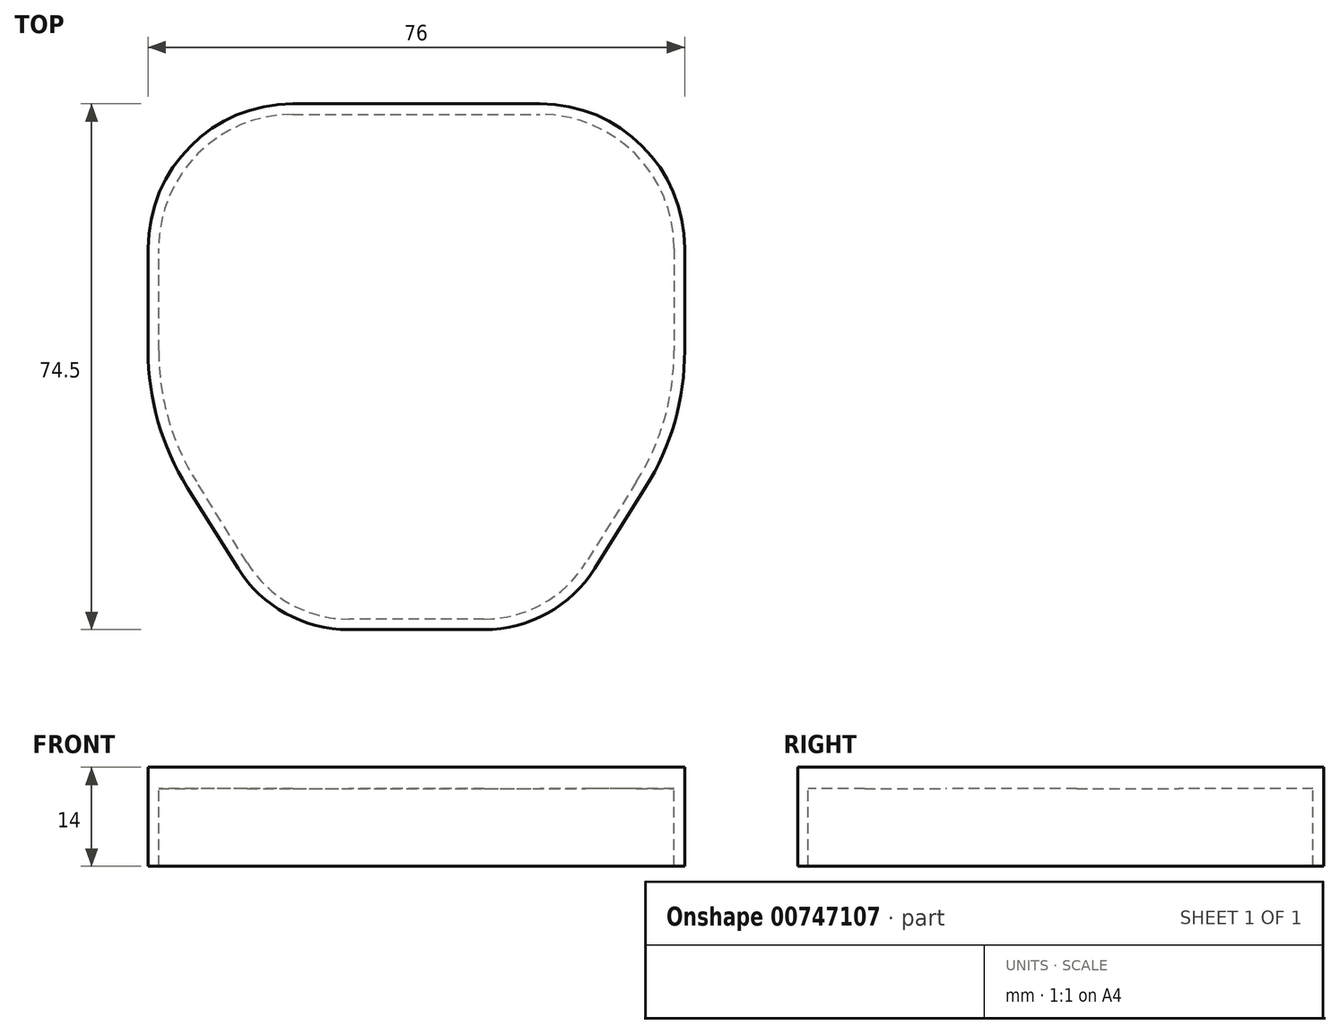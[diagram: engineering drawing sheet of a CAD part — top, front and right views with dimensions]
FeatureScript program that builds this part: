
annotation { "Feature Type Name" : "Feature", "Feature Type Description" : "" }
export const myFeature = defineFeature(function(context is Context, id is Id, definition is map)
    precondition{}
    {
        {
            var Q0;
            Q0=qCreatedBy(makeId("Top.planeOp"),FACE);
            var sketch = newSketch(context, id + "F0", { "sketchPlane" : qUnion([Q0])});
            skLineSegment(sketch, "E0", {"start": v(0, 0) * mm, "end": v(17.5, 0) * mm});
            skLineSegment(sketch, "E1", {"start": v(36.5, -19) * mm, "end": v(36.5, -33.48) * mm});
            skLineSegment(sketch, "E2", {"start": v(31.17, -52.04) * mm, "end": v(24, -63.52) * mm});
            skLineSegment(sketch, "E3", {"start": v(9.58, -71.5) * mm, "end": v(-9.58, -71.5) * mm});
            skLineSegment(sketch, "E4", {"start": v(-24, -63.52) * mm, "end": v(-31.17, -52.04) * mm});
            skLineSegment(sketch, "E5", {"start": v(-36.5, -33.48) * mm, "end": v(-36.5, -19) * mm});
            skLineSegment(sketch, "E6", {"start": v(-17.5, 0) * mm, "end": v(0, 0) * mm});
            skPoint(sketch, "E7.visualSharp", {"position": v(-19, -71.5) * mm});
            skArc(sketch, "E7.filletArc", {"start": v(-24, -63.52) * mm, "mid": v(-17.82, -69.37) * mm, "end": v(-9.58, -71.5) * mm});
            skPoint(sketch, "E8.visualSharp", {"position": v(19, -71.5) * mm});
            skArc(sketch, "E8.filletArc", {"start": v(9.58, -71.5) * mm, "mid": v(17.82, -69.37) * mm, "end": v(24, -63.52) * mm});
            skPoint(sketch, "E9.visualSharp", {"position": v(-36.5, -43.52) * mm});
            skArc(sketch, "E9.filletArc", {"start": v(-36.5, -33.48) * mm, "mid": v(-35.14, -43.13) * mm, "end": v(-31.17, -52.04) * mm});
            skPoint(sketch, "E10.visualSharp", {"position": v(36.5, -43.52) * mm});
            skArc(sketch, "E10.filletArc", {"start": v(31.17, -52.04) * mm, "mid": v(35.14, -43.13) * mm, "end": v(36.5, -33.48) * mm});
            skPoint(sketch, "E11.visualSharp", {"position": v(-36.5, 0) * mm});
            skArc(sketch, "E11.filletArc", {"start": v(-17.5, 0) * mm, "mid": v(-30.94, -5.56) * mm, "end": v(-36.5, -19) * mm});
            skPoint(sketch, "E12.visualSharp", {"position": v(36.5, 0) * mm});
            skArc(sketch, "E12.filletArc", {"start": v(36.5, -19) * mm, "mid": v(30.94, -5.56) * mm, "end": v(17.5, 0) * mm});
            skLineSegment(sketch, "E13.0", {"start": v(-25.27, -64.31) * mm, "end": v(-32.44, -52.83) * mm});
            skArc(sketch, "E13.1", {"start": v(-38, -33.48) * mm, "mid": v(-36.58, -43.55) * mm, "end": v(-32.44, -52.83) * mm});
            skArc(sketch, "E13.2", {"start": v(32.44, -52.83) * mm, "mid": v(36.58, -43.55) * mm, "end": v(38, -33.48) * mm});
            skLineSegment(sketch, "E13.3", {"start": v(32.44, -52.83) * mm, "end": v(25.27, -64.31) * mm});
            skArc(sketch, "E13.4", {"start": v(9.58, -73) * mm, "mid": v(18.55, -70.68) * mm, "end": v(25.27, -64.31) * mm});
            skLineSegment(sketch, "E13.5", {"start": v(9.58, -73) * mm, "end": v(-9.58, -73) * mm});
            skLineSegment(sketch, "E13.6", {"start": v(38, -19) * mm, "end": v(38, -33.48) * mm});
            skArc(sketch, "E13.7", {"start": v(38, -19) * mm, "mid": v(32, -4.5) * mm, "end": v(17.5, 1.5) * mm});
            skArc(sketch, "E13.8", {"start": v(-25.27, -64.31) * mm, "mid": v(-18.55, -70.68) * mm, "end": v(-9.58, -73) * mm});
            skLineSegment(sketch, "E13.9", {"start": v(0, 1.5) * mm, "end": v(17.5, 1.5) * mm});
            skLineSegment(sketch, "E13.10", {"start": v(-17.5, 1.5) * mm, "end": v(0, 1.5) * mm});
            skArc(sketch, "E13.11", {"start": v(-17.5, 1.5) * mm, "mid": v(-32, -4.5) * mm, "end": v(-38, -19) * mm});
            skLineSegment(sketch, "E13.12", {"start": v(-38, -33.48) * mm, "end": v(-38, -19) * mm});
            skSolve(sketch);
        }
        {
            var Q0;
            Q0=makeQuery(id+"F0.imprint","IMPRINT",FACE,{"disambiguationData":[TD([[makeQuery(id+"F0.imprint","IMPRINT",EDGE,{"derivedFrom":sQuery(id+"F0.wireOp",EDGE,"E0")}),-1.0]])]});
            var Q1;
            Q1=makeQuery(id+"F0.imprint","IMPRINT",FACE,{"disambiguationData":[TD([[makeQuery(id+"F0.imprint","IMPRINT",EDGE,{"derivedFrom":sQuery(id+"F0.wireOp",EDGE,"E0")}),1.0]])]});
            var Q2;
            Q2=sQuery(id+"F0.wireOp",EDGE,"E13.11");
            var Q3;
            Q3=sQuery(id+"F0.wireOp",EDGE,"E13.12");
            var Q4;
            Q4=sQuery(id+"F0.wireOp",EDGE,"E13.1");
            var Q5;
            Q5=sQuery(id+"F0.wireOp",EDGE,"E13.0");
            var Q6;
            Q6=sQuery(id+"F0.wireOp",EDGE,"E13.5");
            var Q7;
            Q7=sQuery(id+"F0.wireOp",EDGE,"E13.8");
            var Q8;
            Q8=sQuery(id+"F0.wireOp",EDGE,"E13.4");
            var Q9;
            Q9=sQuery(id+"F0.wireOp",EDGE,"E13.3");
            var Q10;
            Q10=sQuery(id+"F0.wireOp",EDGE,"E13.2");
            var Q11;
            Q11=sQuery(id+"F0.wireOp",EDGE,"E13.6");
            extrude(context, id + "F1", {"entities" : qUnion([Q0, Q1]), "surfaceEntities" : qUnion([Q2, Q3, Q4, Q5, Q6, Q7, Q8, Q9, Q10, Q11]), "depth" : 3 * mm, "offsetDistance" : 25 * mm});
        }
        {
            var Q0;
            Q0 = qSketchRegion(id + "F0", true);
            extrude(context, id + "F2", {"entities" : qUnion([Q0]), "operationType" : NewBodyOperationType.ADD, "oppositeDirection" : true, "depth" : 11 * mm, "offsetDistance" : 25 * mm});
        }
    });
